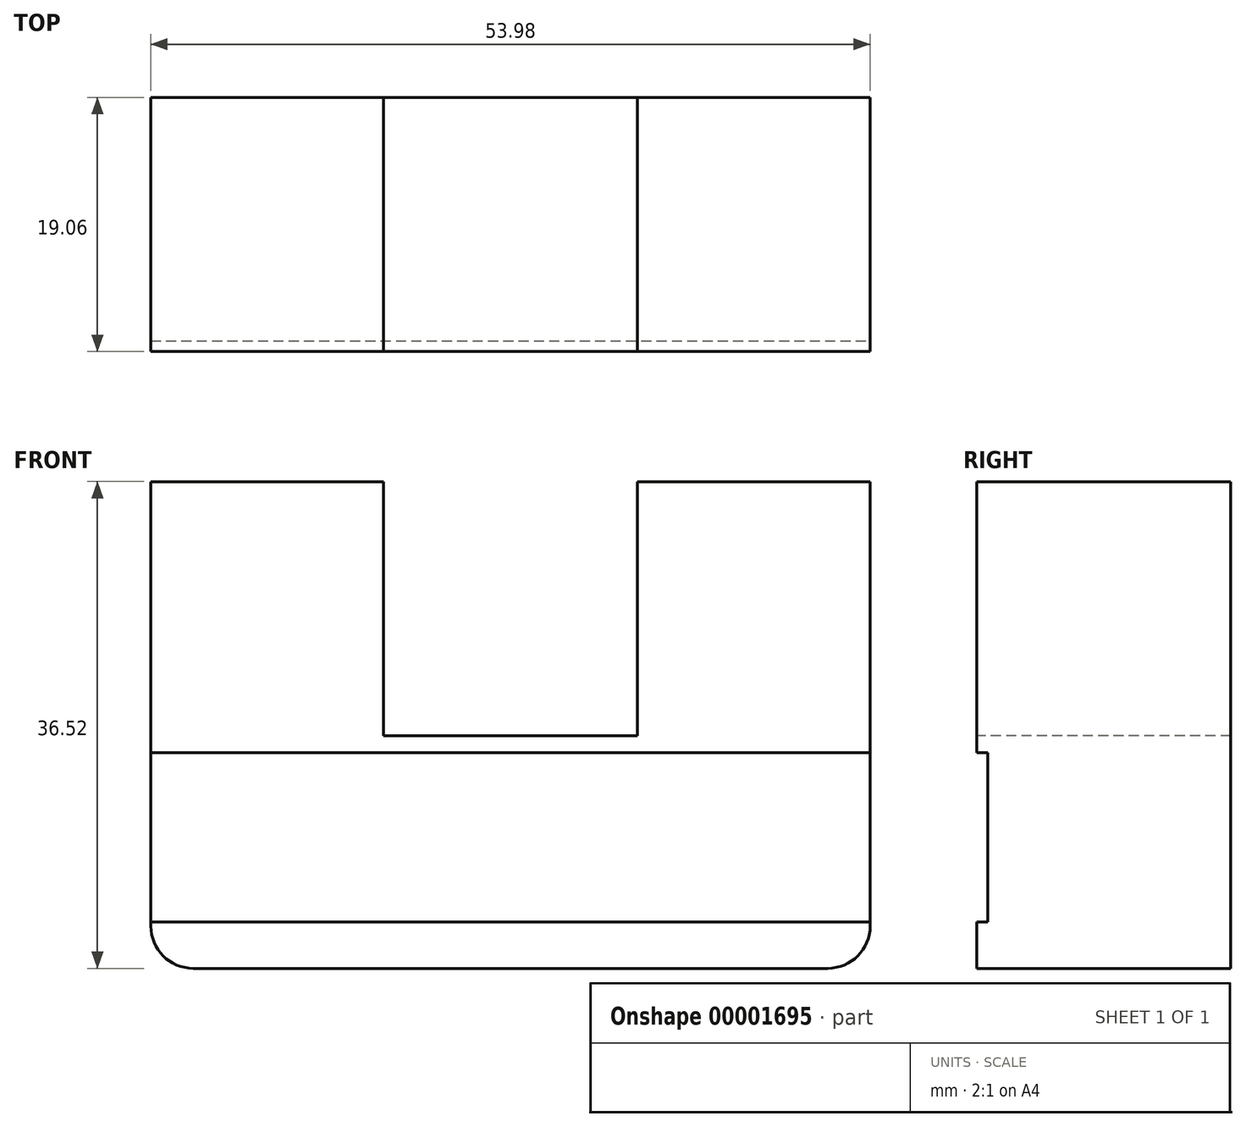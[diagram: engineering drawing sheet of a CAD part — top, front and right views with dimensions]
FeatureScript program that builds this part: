
annotation { "Feature Type Name" : "Feature", "Feature Type Description" : "" }
export const myFeature = defineFeature(function(context is Context, id is Id, definition is map)
    precondition{}
    {
        {
            var Q0;
            Q0=qCreatedBy(makeId("Front.planeOp"),FACE);
            var sketch = newSketch(context, id + "F0", { "sketchPlane" : qUnion([Q0])});
            skLineSegment(sketch, "E0.bottom", {"start": v(-26.99, 26.99) * mm, "end": v(26.99, 26.99) * mm});
            skLineSegment(sketch, "E0.top", {"start": v(-26.99, -26.99) * mm, "end": v(26.99, -26.99) * mm});
            skLineSegment(sketch, "E0.left", {"start": v(-26.99, 26.99) * mm, "end": v(-26.99, -26.99) * mm});
            skLineSegment(sketch, "E0.right", {"start": v(26.99, 26.99) * mm, "end": v(26.99, -26.99) * mm});
            skLineSegment(sketch, "E1", {"start": v(26.99, 26.99) * mm, "end": v(-26.99, -26.99) * mm, "construction": true});
            skSolve(sketch);
        }
        {
            var Q0;
            Q0=qSketchRegion(id+"F0",true);
            extrude(context, id + "F1", {"entities" : qUnion([Q0]), "endBound" : BoundingType.SYMMETRIC, "depth" : 19.05 * mm});
        }
        {
            var Q0;
            Q0=makeQuery(id+"F1.opExtrude","SWEPT_FACE",FACE,{"disambiguationData":[OSD([sQuery(id+"F0.wireOp",EDGE,"E0.bottom")])]});
            var sketch = newSketch(context, id + "F2", { "sketchPlane" : qUnion([Q0])});
            skCircle(sketch, "E2", {"center": v(0, 0) * mm, "radius": 3.97 * mm});
            skSolve(sketch);
        }
        {
            var Q0;
            Q0=makeQuery(id+"F1.opExtrude","CAP_FACE",FACE,{"disambiguationData":[OSD([sQuery(id+"F0.wireOp",EDGE,"E0.bottom"),sQuery(id+"F0.wireOp",EDGE,"E0.top"),sQuery(id+"F0.wireOp",EDGE,"E0.left"),sQuery(id+"F0.wireOp",EDGE,"E0.right")])],"isStart":false});
            var sketch = newSketch(context, id + "F3", { "sketchPlane" : qUnion([Q0])});
            skLineSegment(sketch, "E3.bottom", {"start": v(-9.53, 9.53) * mm, "end": v(9.53, 9.53) * mm});
            skLineSegment(sketch, "E3.top", {"start": v(-9.53, -9.52) * mm, "end": v(9.53, -9.52) * mm});
            skLineSegment(sketch, "E3.left", {"start": v(-9.53, 9.53) * mm, "end": v(-9.53, -9.52) * mm});
            skLineSegment(sketch, "E3.right", {"start": v(9.53, 9.53) * mm, "end": v(9.53, -9.52) * mm});
            skLineSegment(sketch, "E4", {"start": v(9.53, 9.53) * mm, "end": v(-9.53, -9.52) * mm, "construction": true});
            skSolve(sketch);
        }
        {
            var Q0;
            Q0=qSketchRegion(id+"F3",true);
            extrude(context, id + "F4", {"entities" : qUnion([Q0]), "operationType" : NewBodyOperationType.REMOVE, "endBound" : BoundingType.THROUGH_ALL, "oppositeDirection" : true, "depth" : 25.4 * mm});
        }
        {
            var Q0;
            Q0=makeQuery(id+"F2.imprint","IMPRINT",FACE,{"disambiguationData":[TD([[makeQuery(id+"F2.imprint","IMPRINT",EDGE,{"derivedFrom":sQuery(id+"F2.wireOp",EDGE,"E2")}),1.0]])]});
            var Q1;
            Q1=sQuery(id+"F2.wireOp",EDGE,"E2");
            extrude(context, id + "F5", {"entities" : qUnion([Q0]), "operationType" : NewBodyOperationType.REMOVE, "surfaceEntities" : qUnion([Q1]), "endBound" : BoundingType.UP_TO_NEXT, "oppositeDirection" : true, "depth" : 25.4 * mm});
        }
        {
            var Q0;
            Q0=makeQuery(id+"F1.opExtrude","CAP_FACE",FACE,{"disambiguationData":[OSD([sQuery(id+"F0.wireOp",EDGE,"E0.bottom"),sQuery(id+"F0.wireOp",EDGE,"E0.top"),sQuery(id+"F0.wireOp",EDGE,"E0.left"),sQuery(id+"F0.wireOp",EDGE,"E0.right")])],"isStart":false});
            var sketch = newSketch(context, id + "F6", { "sketchPlane" : qUnion([Q0])});
            skArc(sketch, "E5", {"start": v(26.99, 20.64) * mm, "mid": v(0, 26.99) * mm, "end": v(-26.99, 20.64) * mm});
            skLineSegment(sketch, "E6", {"start": v(-26.99, 20.64) * mm, "end": v(26.99, 20.64) * mm, "construction": true});
            skSolve(sketch);
        }
        {
            var Q0;
            Q0=qSketchRegion(id+"F6",true);
            var Q1;
            {var subQ0=makeQuery(id+"F1.opExtrude","CAP_EDGE",EDGE,{"disambiguationData":[OSD([sQuery(id+"F0.wireOp",EDGE,"E0.right")])],"isStart":false});var subQ1=sQuery(id+"F6.wireOp",EDGE,"E5");var subQ2=makeQuery(id+"F6.imprint","INTERSECT",VERTEX,{"derivedFrom":[subQ0,subQ1]});Q1=makeQuery(id+"F6.imprint","IMPRINT",FACE,{"disambiguationData":[TD([[makeQuery(id+"F6.imprint","IMPRINT",EDGE,{"disambiguationData":[TD([[subQ2,-1.0]])],"derivedFrom":subQ1}),-1.0]])]});}
            var Q2;
            {var subQ0=makeQuery(id+"F1.opExtrude","CAP_EDGE",EDGE,{"disambiguationData":[OSD([sQuery(id+"F0.wireOp",EDGE,"E0.left")])],"isStart":false});var subQ1=sQuery(id+"F6.wireOp",EDGE,"E5");var subQ2=makeQuery(id+"F6.imprint","INTERSECT",VERTEX,{"derivedFrom":[subQ0,subQ1]});Q2=makeQuery(id+"F6.imprint","IMPRINT",FACE,{"disambiguationData":[TD([[makeQuery(id+"F6.imprint","IMPRINT",EDGE,{"disambiguationData":[TD([[subQ2,1.0]])],"derivedFrom":subQ1}),-1.0]])]});}
            extrude(context, id + "F7", {"entities" : qUnion([Q0, Q1, Q2]), "operationType" : NewBodyOperationType.REMOVE, "endBound" : BoundingType.THROUGH_ALL, "oppositeDirection" : true, "depth" : 25.4 * mm});
        }
        {
            var Q0;
            Q0=makeQuery(id+"F1.opExtrude","SWEPT_EDGE",EDGE,{"disambiguationData":[OSD([sQuery(id+"F0.wireOp",EDGE,"E0.top"),sQuery(id+"F0.wireOp",EDGE,"E0.right")])]});
            var Q1;
            Q1=makeQuery(id+"F1.opExtrude","SWEPT_EDGE",EDGE,{"disambiguationData":[OSD([sQuery(id+"F0.wireOp",EDGE,"E0.top"),sQuery(id+"F0.wireOp",EDGE,"E0.left")])]});
            var Q2;
            Q2=makeQuery(id+"F7.boolean.opBoolean","COPY",EDGE,{"derivedFrom":makeQuery(id+"F7.opExtrude","SWEPT_EDGE",EDGE,{"disambiguationData":[OSD([sQuery(id+"F0.wireOp",EDGE,"E0.left"),sQuery(id+"F6.wireOp",EDGE,"E5")])]})});
            var Q3;
            Q3=makeQuery(id+"F7.boolean.opBoolean","COPY",EDGE,{"derivedFrom":makeQuery(id+"F7.opExtrude","SWEPT_EDGE",EDGE,{"disambiguationData":[OSD([sQuery(id+"F0.wireOp",EDGE,"E0.right"),sQuery(id+"F6.wireOp",EDGE,"E5")])]})});
            fillet(context, id + "F8", {"entities" : qUnion([Q0, Q1, Q2, Q3]), "radius" : 3.17 * mm, "tangentPropagation" : true, "allowEdgeOverflow" : false});
        }
        {
            var Q0;
            Q0=makeQuery(id+"F1.opExtrude","CAP_FACE",FACE,{"disambiguationData":[OSD([sQuery(id+"F0.wireOp",EDGE,"E0.bottom"),sQuery(id+"F0.wireOp",EDGE,"E0.top"),sQuery(id+"F0.wireOp",EDGE,"E0.left"),sQuery(id+"F0.wireOp",EDGE,"E0.right")])],"isStart":false});
            var sketch = newSketch(context, id + "F9", { "sketchPlane" : qUnion([Q0])});
            skLineSegment(sketch, "E7", {"start": v(-26.99, 9.52) * mm, "end": v(26.99, 9.53) * mm});
            skSolve(sketch);
        }
        {
            var Q0;
            Q0 = qSketchRegion(id + "F9", true);
            var Q1;
            {var subQ3=sQuery(id+"F9.wireOp",EDGE,"E7");var subQ16=makeQuery(id+"F9.imprint","INTERSECT",VERTEX,{"derivedFrom":[makeQuery(id+"F4.boolean.opBoolean","COPY",EDGE,{"derivedFrom":makeQuery(id+"F4.opExtrude","CAP_EDGE",EDGE,{"disambiguationData":[OSD([sQuery(id+"F3.wireOp",EDGE,"E3.left")])],"isStart":true})}),subQ3]});Q1=makeQuery(id+"F9.imprint","IMPRINT",FACE,{"disambiguationData":[TD([[makeQuery(id+"F9.imprint","IMPRINT",EDGE,{"disambiguationData":[TD([[subQ16,1.0]])],"derivedFrom":subQ3}),1.0]])]});}
            extrude(context, id + "F10", {"entities" : qUnion([Q0, Q1]), "operationType" : NewBodyOperationType.REMOVE, "endBound" : BoundingType.THROUGH_ALL, "oppositeDirection" : true, "depth" : 25.4 * mm});
        }
        {
            var Q0;
            Q0=makeQuery(id+"F1.opExtrude","CAP_FACE",FACE,{"disambiguationData":[OSD([sQuery(id+"F0.wireOp",EDGE,"E0.bottom"),sQuery(id+"F0.wireOp",EDGE,"E0.top"),sQuery(id+"F0.wireOp",EDGE,"E0.left"),sQuery(id+"F0.wireOp",EDGE,"E0.right")])],"isStart":false});
            var sketch = newSketch(context, id + "F11", { "sketchPlane" : qUnion([Q0])});
            skLineSegment(sketch, "E8.bottom", {"start": v(-26.99, -10.8) * mm, "end": v(26.99, -10.8) * mm});
            skLineSegment(sketch, "E8.top", {"start": v(-26.99, -23.5) * mm, "end": v(26.99, -23.5) * mm});
            skLineSegment(sketch, "E8.left", {"start": v(-26.99, -10.8) * mm, "end": v(-26.99, -23.5) * mm});
            skLineSegment(sketch, "E8.right", {"start": v(26.99, -10.8) * mm, "end": v(26.99, -23.5) * mm});
            skSolve(sketch);
        }
        {
            var Q0;
            Q0 = qSketchRegion(id + "F11", true);
            extrude(context, id + "F12", {"entities" : qUnion([Q0]), "operationType" : NewBodyOperationType.REMOVE, "oppositeDirection" : true, "depth" : 0.81 * mm});
        }
    });
